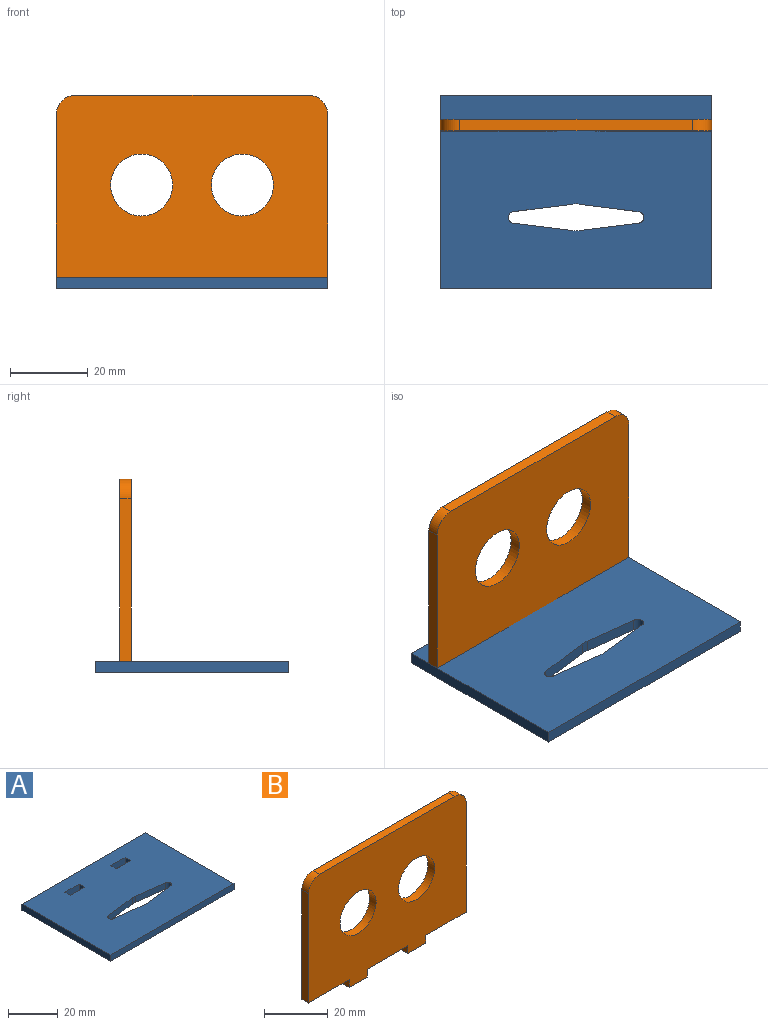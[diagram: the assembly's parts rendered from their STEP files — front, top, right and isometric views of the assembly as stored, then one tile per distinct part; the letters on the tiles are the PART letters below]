
ASSEMBLY  parts=2 mates=1
PART A: 22 faces, bbox 70x50x3 mm
  f0: plane 3x3mm, normal (1,0,0), area 9mm2, adj f1,f19,f20,f21
  f1: plane 8x3mm, normal (0,-1,0), area 24mm2, adj f0,f2,f20,f21
  f2: plane 3x3mm, normal (-1,0,0), area 9mm2, adj f1,f19,f20,f21
  f3: plane 3x3mm, normal (1,0,0), area 9mm2, adj f4,f16,f20,f21
  f4: plane 8x3mm, normal (0,-1,0), area 24mm2, adj f3,f5,f20,f21
  f5: plane 3x3mm, normal (-1,0,0), area 9mm2, adj f4,f16,f20,f21
  f6: plane 50x3mm, normal (-1,0,0), area 150mm2, adj f7,f17,f20,f21
  f7: plane 70x3mm, normal (0,-1,0), area 210mm2, adj f6,f8,f20,f21
  f8: plane 50x3mm, normal (1,0,0), area 150mm2, adj f7,f17,f20,f21
  f9: cylinder r=3.5mm len=3mm, axis (0,0,-1), area 5.2mm2, adj f10,f18,f20,f21
  f10: plane 15.14x3mm, normal (-0.12,-0.99,0), area 45.8mm2, adj f9,f11,f20,f21
  f11: cylinder r=1.5mm len=3mm, axis (0,0,-1), area 14.2mm2, adj f10,f12,f20,f21
  f12: plane 15.1x3mm, normal (-0.12,0.99,0), area 45.7mm2, adj f11,f13,f20,f21
  f13: cylinder r=3.5mm len=3mm, axis (0,0,-1), area 5.2mm2, adj f12,f14,f20,f21
  f14: plane 15.33x3mm, normal (0.12,0.99,0), area 46.3mm2, adj f13,f15,f20,f21
  f15: cylinder r=1.5mm len=3mm, axis (0,0,-1), area 13.4mm2, adj f14,f18,f20,f21
  f16: plane 8x3mm, normal (0,1,0), area 24mm2, adj f3,f5,f20,f21
  f17: plane 70x3mm, normal (0,1,0), area 210mm2, adj f6,f8,f20,f21
  f18: plane 15.2x3mm, normal (0.12,-0.99,0), area 46mm2, adj f9,f15,f20,f21
  f19: plane 8x3mm, normal (0,1,0), area 24mm2, adj f0,f2,f20,f21
  f20: plane 70x50mm, normal (0,0,1), area 3284.8mm2, adj f0,f1,f2,f3,f4,f5,f6,f7
  f21: plane 70x50mm, normal (0,0,-1), area 3284.8mm2, adj f0,f1,f2,f3,f4,f5,f6,f7
PART B: 18 faces, bbox 70x3x50 mm
  f0: plane 3x3mm, normal (1,0,0), area 9mm2, adj f1,f15,f16,f17
  f1: plane 18x3mm, normal (0,0,-1), area 54mm2, adj f0,f2,f16,f17
  f2: plane 3x3mm, normal (-1,0,0), area 9mm2, adj f1,f3,f16,f17
  f3: plane 8x3mm, normal (0,0,-1), area 24mm2, adj f2,f4,f16,f17
  f4: plane 3x3mm, normal (1,0,0), area 9mm2, adj f3,f5,f16,f17
  f5: plane 18x3mm, normal (0,0,-1), area 54mm2, adj f4,f6,f16,f17
  f6: plane 42x3mm, normal (1,0,0), area 126mm2, adj f5,f7,f16,f17
  f7: cylinder r=5mm len=5mm, axis (0,1,0), area 23.6mm2, adj f6,f8,f16,f17
  f8: plane 60x3mm, normal (0,0,1), area 180mm2, adj f7,f9,f16,f17
  f9: cylinder r=5mm len=5mm, axis (0,1,0), area 23.6mm2, adj f8,f10,f16,f17
  f10: plane 42x3mm, normal (-1,0,0), area 126mm2, adj f9,f11,f16,f17
  f11: plane 18x3mm, normal (0,0,-1), area 54mm2, adj f10,f12,f16,f17
  f12: plane 3x3mm, normal (-1,0,0), area 9mm2, adj f11,f15,f16,f17
  f13: cylinder r=8mm len=16mm, axis (0,1,0), area 150.8mm2, adj f16,f17
  f14: cylinder r=8mm len=16mm, axis (0,1,0), area 150.8mm2, adj f16,f17
  f15: plane 8x3mm, normal (0,0,-1), area 24mm2, adj f0,f12,f16,f17
  f16: plane 70x50mm, normal (0,-1,0), area 2925.1mm2, adj f0,f1,f2,f3,f4,f5,f6,f7
  f17: plane 70x50mm, normal (0,1,0), area 2925.1mm2, adj f0,f1,f2,f3,f4,f5,f6,f7
PLACE A t=(-19.12,-22.14,-33.87)mm
PLACE B t=(-15.12,-12.33,-7.08)mm
MATE fastened B.f0 <-> A.f5  axis (1,0,0) through (-28.12,-13.83,-32.37)mm
